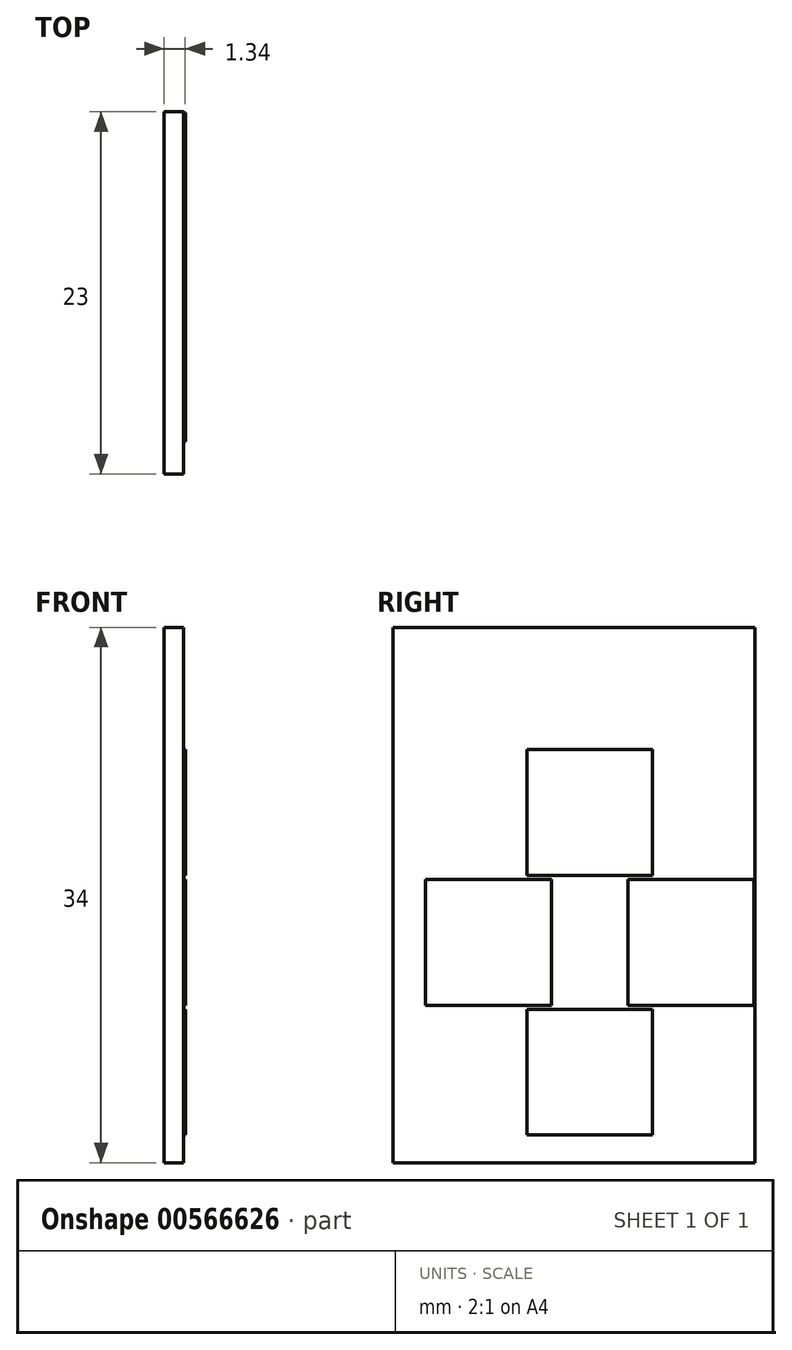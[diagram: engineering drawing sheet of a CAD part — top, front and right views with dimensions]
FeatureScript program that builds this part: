
annotation { "Feature Type Name" : "Feature", "Feature Type Description" : "" }
export const myFeature = defineFeature(function(context is Context, id is Id, definition is map)
    precondition{}
    {
        {
            var Q0;
            Q0=qCreatedBy(makeId("Right.planeOp"),FACE);
            var sketch = newSketch(context, id + "F0", { "sketchPlane" : qUnion([Q0])});
            skLineSegment(sketch, "E0.bottom", {"start": v(-11.5, 17) * mm, "end": v(11.5, 17) * mm});
            skLineSegment(sketch, "E0.top", {"start": v(-11.5, -17) * mm, "end": v(11.5, -17) * mm});
            skLineSegment(sketch, "E0.left", {"start": v(-11.5, 17) * mm, "end": v(-11.5, -17) * mm});
            skLineSegment(sketch, "E0.right", {"start": v(11.5, 17) * mm, "end": v(11.5, -17) * mm});
            skPoint(sketch, "E0.middle", {"position": v(0, 0) * mm});
            skSolve(sketch);
        }
        {
            var Q0;
            Q0=makeQuery(id+"F0.imprint","IMPRINT",FACE,{"disambiguationData":[TD([[makeQuery(id+"F0.imprint","IMPRINT",EDGE,{"derivedFrom":sQuery(id+"F0.wireOp",EDGE,"E0.bottom")}),-1.0]])]});
            extrude(context, id + "F1", {"entities" : qUnion([Q0]), "endBound" : BoundingType.SYMMETRIC, "depth" : 1.25 * mm, "offsetDistance" : 25 * mm});
        }
        {
            var Q0;
            Q0=makeQuery(id+"F1.opExtrude","CAP_FACE",FACE,{"disambiguationData":[OSD([sQuery(id+"F0.wireOp",EDGE,"E0.bottom"),sQuery(id+"F0.wireOp",EDGE,"E0.top"),sQuery(id+"F0.wireOp",EDGE,"E0.left"),sQuery(id+"F0.wireOp",EDGE,"E0.right")])],"isStart":false});
            var sketch = newSketch(context, id + "F2", { "sketchPlane" : qUnion([Q0])});
            skLineSegment(sketch, "E1.bottom", {"start": v(-2.38, 6.5) * mm, "end": v(4.37, 6.5) * mm, "construction": true});
            skLineSegment(sketch, "E1.top", {"start": v(-2.38, -12.5) * mm, "end": v(4.37, -12.5) * mm, "construction": true});
            skLineSegment(sketch, "E1.left", {"start": v(-2.38, 6.5) * mm, "end": v(-2.38, -12.5) * mm, "construction": true});
            skLineSegment(sketch, "E1.right", {"start": v(4.37, 6.5) * mm, "end": v(4.37, -12.5) * mm, "construction": true});
            skPoint(sketch, "E1.middle", {"position": v(1, -3) * mm});
            skLineSegment(sketch, "E2.bottom", {"start": v(-8.5, 0.37) * mm, "end": v(10.5, 0.37) * mm, "construction": true});
            skLineSegment(sketch, "E2.top", {"start": v(-8.5, -6.38) * mm, "end": v(10.5, -6.38) * mm, "construction": true});
            skLineSegment(sketch, "E2.left", {"start": v(-8.5, 0.37) * mm, "end": v(-8.5, -6.38) * mm, "construction": true});
            skLineSegment(sketch, "E2.right", {"start": v(10.5, 0.37) * mm, "end": v(10.5, -6.38) * mm, "construction": true});
            skLineSegment(sketch, "E3.bottom", {"start": v(-9.44, 1) * mm, "end": v(-1.44, 1) * mm});
            skLineSegment(sketch, "E3.top", {"start": v(-9.44, -7) * mm, "end": v(-1.44, -7) * mm});
            skLineSegment(sketch, "E3.left", {"start": v(-9.44, 1) * mm, "end": v(-9.44, -7) * mm});
            skLineSegment(sketch, "E3.right", {"start": v(-1.44, 1) * mm, "end": v(-1.44, -7) * mm});
            skPoint(sketch, "E3.middle", {"position": v(-5.44, -3) * mm});
            skPoint(sketch, "E3.middle.positionSnap0", {"position": v(-8.5, -3) * mm});
            skPoint(sketch, "E3.centerSnap0", {"position": v(-8.5, -3) * mm});
            skLineSegment(sketch, "E4.bottom", {"start": v(3.44, 1) * mm, "end": v(11.44, 1) * mm});
            skLineSegment(sketch, "E4.top", {"start": v(3.44, -7) * mm, "end": v(11.44, -7) * mm});
            skLineSegment(sketch, "E4.left", {"start": v(3.44, 1) * mm, "end": v(3.44, -7) * mm});
            skLineSegment(sketch, "E4.right", {"start": v(11.44, 1) * mm, "end": v(11.44, -7) * mm});
            skPoint(sketch, "E4.middle", {"position": v(7.44, -3) * mm});
            skPoint(sketch, "E4.middle.positionSnap0", {"position": v(10.5, -3) * mm});
            skPoint(sketch, "E4.centerSnap0", {"position": v(10.5, -3) * mm});
            skLineSegment(sketch, "E5.bottom", {"start": v(-3, 9.25) * mm, "end": v(5, 9.25) * mm});
            skLineSegment(sketch, "E5.top", {"start": v(-3, 1.25) * mm, "end": v(5, 1.25) * mm});
            skLineSegment(sketch, "E5.left", {"start": v(-3, 9.25) * mm, "end": v(-3, 1.25) * mm});
            skLineSegment(sketch, "E5.right", {"start": v(5, 9.25) * mm, "end": v(5, 1.25) * mm});
            skPoint(sketch, "E5.middle", {"position": v(1, 5.25) * mm});
            skPoint(sketch, "E5.middle.positionSnap0", {"position": v(1, 6.5) * mm});
            skPoint(sketch, "E5.centerSnap0", {"position": v(1, 6.5) * mm});
            skLineSegment(sketch, "E6.bottom", {"start": v(-3, -7.25) * mm, "end": v(5, -7.25) * mm});
            skLineSegment(sketch, "E6.top", {"start": v(-3, -15.25) * mm, "end": v(5, -15.25) * mm});
            skLineSegment(sketch, "E6.left", {"start": v(-3, -7.25) * mm, "end": v(-3, -15.25) * mm});
            skLineSegment(sketch, "E6.right", {"start": v(5, -7.25) * mm, "end": v(5, -15.25) * mm});
            skPoint(sketch, "E6.middle", {"position": v(1, -11.25) * mm});
            skPoint(sketch, "E6.middle.positionSnap0", {"position": v(1, -12.5) * mm});
            skPoint(sketch, "E6.centerSnap0", {"position": v(1, -12.5) * mm});
            skSolve(sketch);
        }
        {
            var Q0;
            Q0=qSketchRegion(id+"F2",true);
            extrude(context, id + "F3", {"entities" : qUnion([Q0]), "operationType" : NewBodyOperationType.ADD, "depth" : .1 * mm, "offsetDistance" : 25 * mm});
        }
    });
